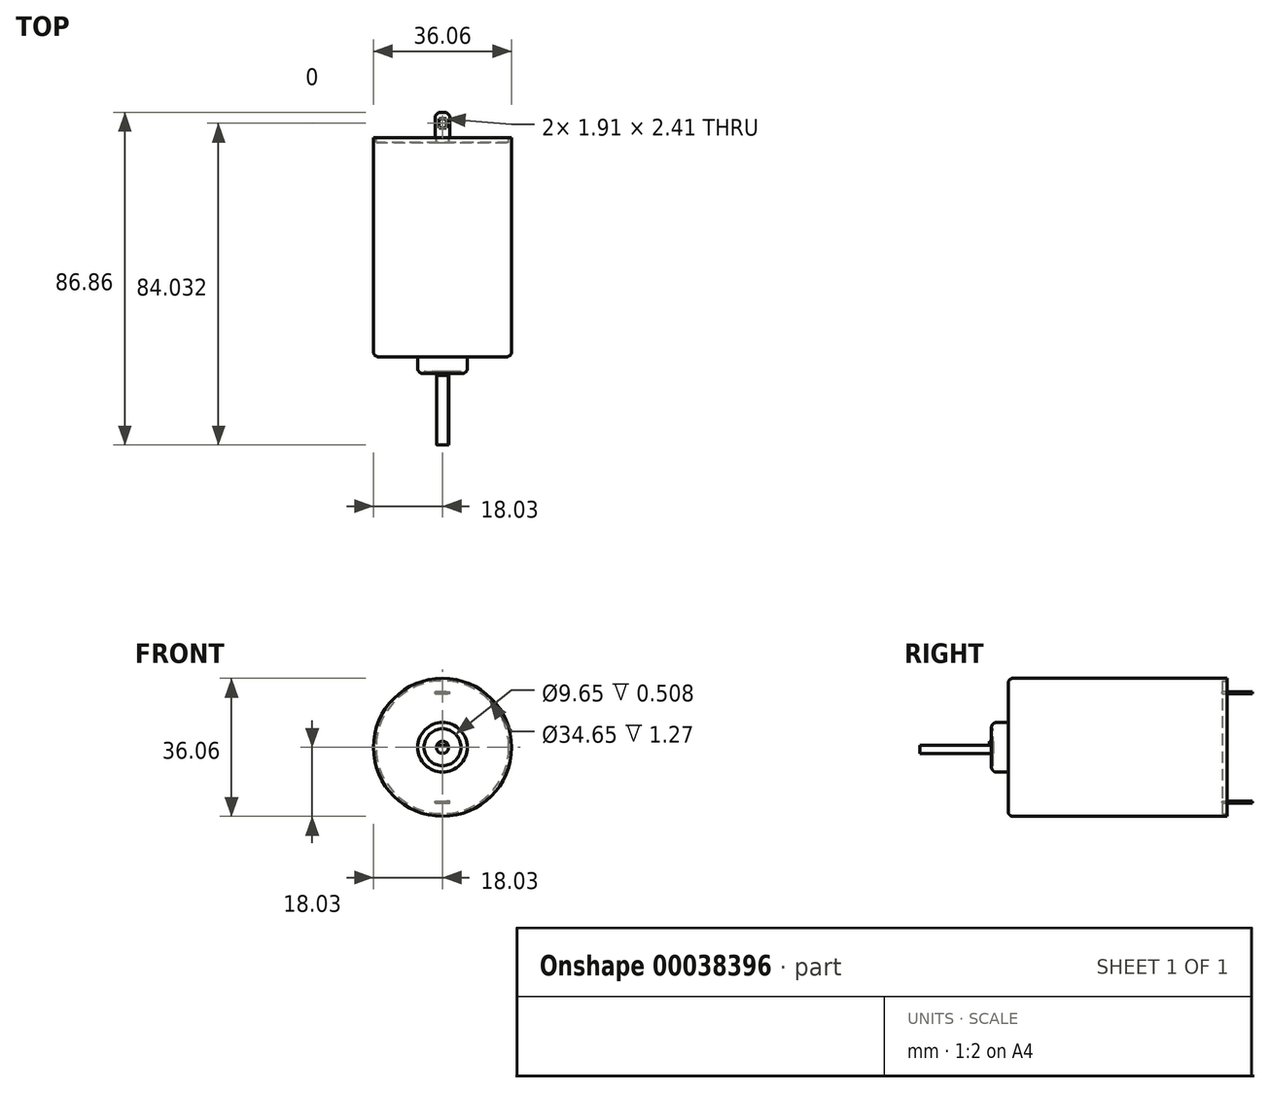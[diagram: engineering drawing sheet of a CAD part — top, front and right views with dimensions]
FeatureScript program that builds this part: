
annotation { "Feature Type Name" : "Feature", "Feature Type Description" : "" }
export const myFeature = defineFeature(function(context is Context, id is Id, definition is map)
    precondition{}
    {
        {
            var Q0;
            Q0=qCreatedBy(makeId("Front.planeOp"),FACE);
            var sketch = newSketch(context, id + "F0", { "sketchPlane" : qUnion([Q0])});
            skCircle(sketch, "E0", {"center": v(0, 0) * mm, "radius": 18.03 * mm});
            skSolve(sketch);
        }
        {
            var Q0;
            Q0 = qSketchRegion(id + "F0", true);
            extrude(context, id + "F1", {"entities" : qUnion([Q0]), "depth" : 57.25 * mm});
        }
        {
            var Q0;
            Q0=makeQuery(id+"F1.opExtrude","CAP_FACE",FACE,{"disambiguationData":[OSD([sQuery(id+"F0.wireOp",EDGE,"E0")])],"isStart":false});
            var sketch = newSketch(context, id + "F2", { "sketchPlane" : qUnion([Q0])});
            skCircle(sketch, "E1", {"center": v(0, 0) * mm, "radius": 6.48 * mm});
            skSolve(sketch);
        }
        {
            var Q0;
            Q0=makeQuery(id+"F2.imprint","IMPRINT",FACE,{"disambiguationData":[TD([[makeQuery(id+"F2.imprint","IMPRINT",EDGE,{"derivedFrom":sQuery(id+"F2.wireOp",EDGE,"E1")}),1.0]])]});
            extrude(context, id + "F3", {"entities" : qUnion([Q0]), "operationType" : NewBodyOperationType.ADD, "depth" : 4.34 * mm});
        }
        {
            var Q0;
            Q0=makeQuery(id+"F3.opExtrude","CAP_EDGE",EDGE,{"disambiguationData":[OSD([sQuery(id+"F2.wireOp",EDGE,"E1")])],"isStart":true});
            var Q1;
            Q1=makeQuery(id+"F3.opExtrude","CAP_EDGE",EDGE,{"disambiguationData":[OSD([sQuery(id+"F2.wireOp",EDGE,"E1")])],"isStart":false});
            fillet(context, id + "F4", {"entities" : qUnion([Q0, Q1]), "radius" : 1.27 * mm, "tangentPropagation" : true, "allowEdgeOverflow" : false});
        }
        {
            var Q0;
            Q0=makeQuery(id+"F3.opExtrude","CAP_FACE",FACE,{"disambiguationData":[OSD([sQuery(id+"F2.wireOp",EDGE,"E1")])],"isStart":false});
            var sketch = newSketch(context, id + "F5", { "sketchPlane" : qUnion([Q0])});
            skCircle(sketch, "E2", {"center": v(0, 0) * mm, "radius": 4.83 * mm});
            skSolve(sketch);
        }
        {
            var Q0;
            Q0 = qSketchRegion(id + "F5", true);
            extrude(context, id + "F6", {"entities" : qUnion([Q0]), "operationType" : NewBodyOperationType.REMOVE, "oppositeDirection" : true, "depth" : 0.5 * mm});
        }
        {
            var Q0;
            Q0=makeQuery(id+"F6.boolean.opBoolean","COPY",FACE,{"derivedFrom":makeQuery(id+"F6.opExtrude","CAP_FACE",FACE,{"disambiguationData":[OSD([sQuery(id+"F5.wireOp",EDGE,"E2")])],"isStart":false})});
            var sketch = newSketch(context, id + "F7", { "sketchPlane" : qUnion([Q0])});
            skCircle(sketch, "E3", {"center": v(0, 0) * mm, "radius": 1.59 * mm});
            skSolve(sketch);
        }
        {
            var Q0;
            Q0=makeQuery(id+"F7.imprint","IMPRINT",FACE,{"disambiguationData":[TD([[makeQuery(id+"F7.imprint","IMPRINT",EDGE,{"derivedFrom":sQuery(id+"F7.wireOp",EDGE,"E3")}),1.0]])]});
            extrude(context, id + "F8", {"entities" : qUnion([Q0]), "operationType" : NewBodyOperationType.ADD, "depth" : 19.18 * mm});
        }
        {
            var Q0;
            Q0=qCreatedBy(makeId("Right.planeOp"),FACE);
            var sketch = newSketch(context, id + "F9", { "sketchPlane" : qUnion([Q0])});
            skLineSegment(sketch, "E4", {"start": v(0, 0) * mm, "end": v(-103.6, 0) * mm, "construction": true});
            skLineSegment(sketch, "E5", {"start": v(-80.26, 1.59) * mm, "end": v(-61.09, 1.59) * mm, "construction": true});
            skLineSegment(sketch, "E6.0", {"start": v(-80.26, -1.59) * mm, "end": v(-80.26, 1.59) * mm, "construction": true});
            skLineSegment(sketch, "E7", {"start": v(-61.09, -1.59) * mm, "end": v(-80.26, -1.59) * mm, "construction": true});
            skLineSegment(sketch, "E8", {"start": v(-80.26, 0.57) * mm, "end": v(-62.1, 0.57) * mm});
            skLineSegment(sketch, "E9", {"start": v(-61.6, -5.2) * mm, "end": v(-61.6, 5.2) * mm});
            skLineSegment(sketch, "E10", {"start": v(-62.1, 0.57) * mm, "end": v(-62.1, 1.59) * mm});
            skLineSegment(sketch, "E11", {"start": v(-62.1, 1.59) * mm, "end": v(-80.26, 1.59) * mm});
            skLineSegment(sketch, "E12", {"start": v(-80.26, 1.59) * mm, "end": v(-80.26, 0.57) * mm});
            skSolve(sketch);
        }
        {
            var Q0;
            Q0 = qSketchRegion(id + "F9", true);
            extrude(context, id + "F10", {"entities" : qUnion([Q0]), "operationType" : NewBodyOperationType.REMOVE, "endBound" : BoundingType.SYMMETRIC, "depth" : 6.35 * mm});
        }
        {
            var Q0;
            Q0=makeQuery(id+"F1.opExtrude","CAP_FACE",FACE,{"disambiguationData":[OSD([sQuery(id+"F0.wireOp",EDGE,"E0")])],"isStart":true});
            var sketch = newSketch(context, id + "F11", { "sketchPlane" : qUnion([Q0])});
            skCircle(sketch, "E13", {"center": v(0, 0) * mm, "radius": 17.32 * mm});
            skSolve(sketch);
        }
        {
            var Q0;
            Q0 = qSketchRegion(id + "F11", true);
            extrude(context, id + "F12", {"entities" : qUnion([Q0]), "operationType" : NewBodyOperationType.REMOVE, "oppositeDirection" : true, "depth" : 1.27 * mm});
        }
        {
            var Q0;
            Q0=makeQuery(id+"F12.boolean.opBoolean","COPY",FACE,{"derivedFrom":makeQuery(id+"F12.opExtrude","CAP_FACE",FACE,{"disambiguationData":[OSD([sQuery(id+"F11.wireOp",EDGE,"E13")])],"isStart":false})});
            var sketch = newSketch(context, id + "F13", { "sketchPlane" : qUnion([Q0])});
            skLineSegment(sketch, "E14", {"start": v(0, 17.32) * mm, "end": v(0, -17.32) * mm, "construction": true});
            skLineSegment(sketch, "E15", {"start": v(-17.32, 0) * mm, "end": v(17.32, 0) * mm, "construction": true});
            skLineSegment(sketch, "E16.rect.bottom", {"start": v(1.9, 14.02) * mm, "end": v(-1.9, 14.02) * mm});
            skLineSegment(sketch, "E16.rect.top", {"start": v(1.9, 14.53) * mm, "end": v(-1.9, 14.53) * mm});
            skLineSegment(sketch, "E16.rect.left", {"start": v(1.9, 14.02) * mm, "end": v(1.9, 14.53) * mm});
            skLineSegment(sketch, "E16.rect.right", {"start": v(-1.9, 14.02) * mm, "end": v(-1.9, 14.53) * mm});
            skPoint(sketch, "E16.rect.middle", {"position": v(0, 14.27) * mm});
            skLineSegment(sketch, "E17.MirrorCS", {"start": v(1.9, -14.02) * mm, "end": v(-1.9, -14.02) * mm});
            skLineSegment(sketch, "E18.MirrorCS", {"start": v(1.9, -14.53) * mm, "end": v(-1.9, -14.53) * mm});
            skLineSegment(sketch, "E19.MirrorCS", {"start": v(1.9, -14.02) * mm, "end": v(1.9, -14.53) * mm});
            skPoint(sketch, "E20.MirrorP", {"position": v(0, -14.27) * mm});
            skLineSegment(sketch, "E21.MirrorCS", {"start": v(-1.9, -14.02) * mm, "end": v(-1.9, -14.53) * mm});
            skSolve(sketch);
        }
        {
            var Q0;
            Q0=makeQuery(id+"F13.imprint","IMPRINT",FACE,{"disambiguationData":[TD([[makeQuery(id+"F13.imprint","IMPRINT",EDGE,{"derivedFrom":sQuery(id+"F13.wireOp",EDGE,"E16.rect.bottom")}),-1.0]])]});
            var Q1;
            Q1=makeQuery(id+"F13.imprint","IMPRINT",FACE,{"disambiguationData":[TD([[makeQuery(id+"F13.imprint","IMPRINT",EDGE,{"derivedFrom":sQuery(id+"F13.wireOp",EDGE,"E17.MirrorCS")}),1.0]])]});
            extrude(context, id + "F14", {"entities" : qUnion([Q0, Q1]), "operationType" : NewBodyOperationType.ADD, "depth" : 7.87 * mm});
        }
        {
            var Q0;
            Q0=makeQuery(id+"F14.opExtrude","SWEPT_FACE",FACE,{"disambiguationData":[OSD([sQuery(id+"F13.wireOp",EDGE,"E16.rect.bottom")])]});
            var sketch = newSketch(context, id + "F15", { "sketchPlane" : qUnion([Q0])});
            skLineSegment(sketch, "E22.rect.bottom", {"start": v(0.95, -4.98) * mm, "end": v(-0.95, -4.98) * mm});
            skLineSegment(sketch, "E22.rect.top", {"start": v(0.95, -2.57) * mm, "end": v(-0.95, -2.57) * mm});
            skLineSegment(sketch, "E22.rect.left", {"start": v(0.95, -4.98) * mm, "end": v(0.95, -2.57) * mm});
            skLineSegment(sketch, "E22.rect.right", {"start": v(-0.95, -4.98) * mm, "end": v(-0.95, -2.57) * mm});
            skPoint(sketch, "E22.rect.middle", {"position": v(0, -3.77) * mm});
            skPoint(sketch, "E22.rect.middle.positionSnap0", {"position": v(0, -6.6) * mm});
            skPoint(sketch, "E22.rect.centerSnap0", {"position": v(0, -6.6) * mm});
            skLineSegment(sketch, "E23.rect.bottom", {"start": v(-1.61, 1.27) * mm, "end": v(1.61, 1.27) * mm});
            skLineSegment(sketch, "E23.rect.top", {"start": v(-1.61, -0.25) * mm, "end": v(1.61, -0.25) * mm, "construction": true});
            skLineSegment(sketch, "E23.rect.left", {"start": v(-1.61, 1.27) * mm, "end": v(-1.61, -0.25) * mm, "construction": true});
            skLineSegment(sketch, "E23.rect.right", {"start": v(1.61, 1.27) * mm, "end": v(1.61, -0.25) * mm, "construction": true});
            skPoint(sketch, "E23.rect.middle", {"position": v(0, 0.5) * mm});
            skLineSegment(sketch, "E24.0", {"start": v(-1.9, 1.27) * mm, "end": v(1.9, 1.27) * mm});
            skLineSegment(sketch, "E25.bottom", {"start": v(1.61, -0.25) * mm, "end": v(1.9, -0.25) * mm});
            skLineSegment(sketch, "E25.top", {"start": v(1.61, 1.27) * mm, "end": v(1.9, 1.27) * mm});
            skLineSegment(sketch, "E25.left", {"start": v(1.61, -0.25) * mm, "end": v(1.61, 1.27) * mm});
            skLineSegment(sketch, "E25.right", {"start": v(1.9, -0.25) * mm, "end": v(1.9, 1.27) * mm});
            skLineSegment(sketch, "E26.bottom", {"start": v(-1.61, -0.25) * mm, "end": v(-1.9, -0.25) * mm});
            skLineSegment(sketch, "E26.top", {"start": v(-1.61, 1.27) * mm, "end": v(-1.9, 1.27) * mm});
            skLineSegment(sketch, "E26.left", {"start": v(-1.61, -0.25) * mm, "end": v(-1.61, 1.27) * mm});
            skLineSegment(sketch, "E26.right", {"start": v(-1.9, -0.25) * mm, "end": v(-1.9, 1.27) * mm});
            skSolve(sketch);
        }
        {
            var Q0;
            Q0=makeQuery(id+"F14.opExtrude","CAP_EDGE",EDGE,{"disambiguationData":[OSD([sQuery(id+"F13.wireOp",EDGE,"E16.rect.left")])],"isStart":false});
            var Q1;
            Q1=makeQuery(id+"F14.opExtrude","CAP_EDGE",EDGE,{"disambiguationData":[OSD([sQuery(id+"F13.wireOp",EDGE,"E16.rect.right")])],"isStart":false});
            var Q2;
            Q2=makeQuery(id+"F14.opExtrude","CAP_EDGE",EDGE,{"disambiguationData":[OSD([sQuery(id+"F13.wireOp",EDGE,"E19.MirrorCS")])],"isStart":false});
            var Q3;
            Q3=makeQuery(id+"F14.opExtrude","CAP_EDGE",EDGE,{"disambiguationData":[OSD([sQuery(id+"F13.wireOp",EDGE,"E21.MirrorCS")])],"isStart":false});
            chamfer(context, id + "F16", {"entities" : qUnion([Q0, Q1, Q2, Q3]), "width" : 0.89 * mm, "tangentPropagation" : true});
        }
        {
            var Q0;
            Q0=makeQuery(id+"F1.opExtrude","CAP_EDGE",EDGE,{"disambiguationData":[OSD([sQuery(id+"F0.wireOp",EDGE,"E0")])],"isStart":false});
            fillet(context, id + "F17", {"entities" : qUnion([Q0]), "radius" : 1.27 * mm, "tangentPropagation" : true, "allowEdgeOverflow" : false});
        }
        {
            var Q0;
            Q0=makeQuery(id+"F14.opExtrude","SWEPT_FACE",FACE,{"disambiguationData":[OSD([sQuery(id+"F13.wireOp",EDGE,"E16.rect.top")])]});
            var sketch = newSketch(context, id + "F18", { "sketchPlane" : qUnion([Q0])});
            skLineSegment(sketch, "E27.0", {"start": v(0.95, 4.98) * mm, "end": v(0.95, 2.57) * mm});
            skLineSegment(sketch, "E28.0", {"start": v(0.95, 4.98) * mm, "end": v(-0.95, 4.98) * mm});
            skLineSegment(sketch, "E29.0", {"start": v(-0.95, 4.98) * mm, "end": v(-0.95, 2.57) * mm});
            skLineSegment(sketch, "E30.0", {"start": v(0.95, 2.57) * mm, "end": v(-0.95, 2.57) * mm});
            skLineSegment(sketch, "E31.0", {"start": v(-1.61, 0.25) * mm, "end": v(-1.61, -1.27) * mm});
            skLineSegment(sketch, "E32.0", {"start": v(-1.9, 0.25) * mm, "end": v(-1.9, -1.27) * mm});
            skLineSegment(sketch, "E33.0", {"start": v(-1.61, 0.25) * mm, "end": v(-1.9, 0.25) * mm});
            skLineSegment(sketch, "E34.1", {"start": v(1.61, 0.25) * mm, "end": v(1.61, -1.27) * mm});
            skLineSegment(sketch, "E34.2", {"start": v(1.61, 0.25) * mm, "end": v(1.9, 0.25) * mm});
            skLineSegment(sketch, "E34.3", {"start": v(1.9, 0.25) * mm, "end": v(1.9, -1.27) * mm});
            skLineSegment(sketch, "E35", {"start": v(-1.9, -1.27) * mm, "end": v(-1.61, -1.27) * mm});
            skLineSegment(sketch, "E36", {"start": v(1.61, -1.27) * mm, "end": v(1.9, -1.27) * mm});
            skSolve(sketch);
        }
        {
            var Q0;
            Q0=makeQuery(id+"F18.imprint","IMPRINT",FACE,{"disambiguationData":[TD([[makeQuery(id+"F18.imprint","IMPRINT",EDGE,{"derivedFrom":sQuery(id+"F18.wireOp",EDGE,"E31.0")}),-1.0]])]});
            var Q1;
            Q1=makeQuery(id+"F18.imprint","IMPRINT",FACE,{"disambiguationData":[TD([[makeQuery(id+"F18.imprint","IMPRINT",EDGE,{"derivedFrom":sQuery(id+"F18.wireOp",EDGE,"E34.1")}),1.0]])]});
            var Q2;
            Q2=makeQuery(id+"F18.imprint","IMPRINT",FACE,{"disambiguationData":[TD([[makeQuery(id+"F18.imprint","IMPRINT",EDGE,{"derivedFrom":sQuery(id+"F18.wireOp",EDGE,"E27.0")}),-1.0]])]});
            extrude(context, id + "F19", {"entities" : qUnion([Q0, Q1, Q2]), "operationType" : NewBodyOperationType.REMOVE, "oppositeDirection" : true, "depth" : 29.1 * mm});
        }
    });
